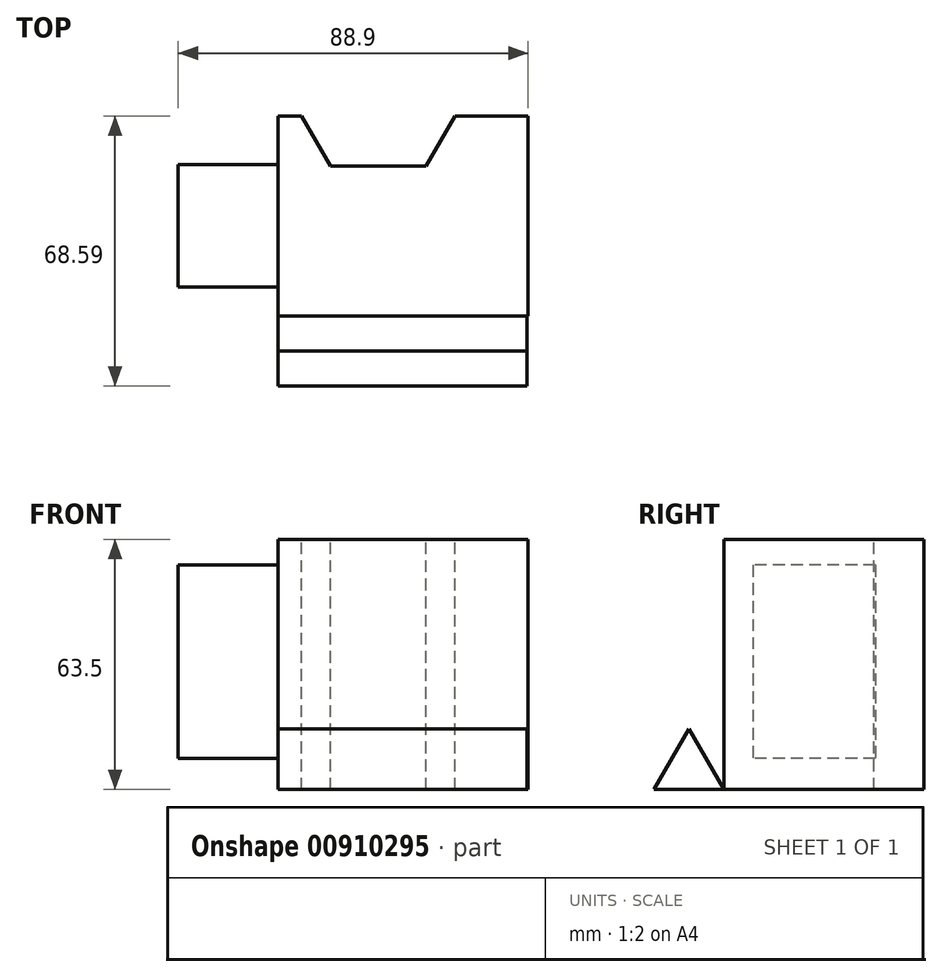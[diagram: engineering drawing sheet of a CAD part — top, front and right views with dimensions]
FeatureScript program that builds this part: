
annotation { "Feature Type Name" : "Feature", "Feature Type Description" : "" }
export const myFeature = defineFeature(function(context is Context, id is Id, definition is map)
    precondition{}
    {
        {
            var Q0;
            Q0=qCreatedBy(makeId("Front.planeOp"),FACE);
            var sketch = newSketch(context, id + "F0", { "sketchPlane" : qUnion([Q0])});
            skLineSegment(sketch, "E0.bottom", {"start": v(-31.75, 31.75) * mm, "end": v(31.75, 31.75) * mm});
            skLineSegment(sketch, "E0.top", {"start": v(-31.75, -31.75) * mm, "end": v(31.75, -31.75) * mm});
            skLineSegment(sketch, "E0.left", {"start": v(-31.75, 31.75) * mm, "end": v(-31.75, -31.75) * mm});
            skLineSegment(sketch, "E0.right", {"start": v(31.75, 31.75) * mm, "end": v(31.75, -31.75) * mm});
            skPoint(sketch, "E0.middle", {"position": v(0, 0) * mm});
            skSolve(sketch);
        }
        {
            var Q0;
            Q0=makeQuery(id+"F0.imprint","IMPRINT",FACE,{"disambiguationData":[TD([[makeQuery(id+"F0.imprint","IMPRINT",EDGE,{"derivedFrom":sQuery(id+"F0.wireOp",EDGE,"E0.bottom")}),-1.0]])]});
            extrude(context, id + "F1", {"entities" : qUnion([Q0]), "depth" : 50.8 * mm, "offsetDistance" : 25.4 * mm});
        }
        {
            var Q0;
            Q0=makeQuery(id+"F1.opExtrude","SWEPT_FACE",FACE,{"disambiguationData":[OSD([sQuery(id+"F0.wireOp",EDGE,"E0.bottom")])]});
            var sketch = newSketch(context, id + "F2", { "sketchPlane" : qUnion([Q0])});
            skLineSegment(sketch, "E1", {"start": v(-25.83, 0) * mm, "end": v(-18.5, -12.7) * mm});
            skLineSegment(sketch, "E2", {"start": v(-18.5, -12.7) * mm, "end": v(5.8, -12.7) * mm});
            skLineSegment(sketch, "E3", {"start": v(5.8, -12.7) * mm, "end": v(13.13, 0) * mm});
            skLineSegment(sketch, "E4", {"start": v(13.13, 0) * mm, "end": v(-25.83, 0) * mm});
            skLineSegment(sketch, "E5", {"start": v(-6.35, -12.7) * mm, "end": v(-6.35, 0) * mm, "construction": true});
            skSolve(sketch);
        }
        {
            var Q0;
            Q0=makeQuery(id+"F2.imprint","IMPRINT",FACE,{"disambiguationData":[TD([[makeQuery(id+"F2.imprint","IMPRINT",EDGE,{"derivedFrom":sQuery(id+"F2.wireOp",EDGE,"E1")}),1.0]])]});
            extrude(context, id + "F3", {"entities" : qUnion([Q0]), "operationType" : NewBodyOperationType.REMOVE, "oppositeDirection" : true, "depth" : 82.04 * mm, "offsetDistance" : 25.4 * mm});
        }
        {
            var Q0;
            Q0=makeQuery(id+"F1.opExtrude","SWEPT_FACE",FACE,{"disambiguationData":[OSD([sQuery(id+"F0.wireOp",EDGE,"E0.left")])]});
            var sketch = newSketch(context, id + "F4", { "sketchPlane" : qUnion([Q0])});
            skSolve(sketch);
        }
        {
            var Q0;
            {var subQ0=sQuery(id+"F0.wireOp",EDGE,"E0.left");Q0=makeQuery(id+"F4.imprint","IMPRINT",FACE,{"disambiguationData":[TD([[makeQuery(id+"F4.imprint","IMPRINT",EDGE,{"derivedFrom":makeQuery(id+"F1.opExtrude","CAP_EDGE",EDGE,{"disambiguationData":[OSD([subQ0])],"isStart":true})}),1.0]])]});}
            var sketch = newSketch(context, id + "F5", { "sketchPlane" : qUnion([Q0])});
            skLineSegment(sketch, "E6", {"start": v(50.8, -31.75) * mm, "end": v(59.7, -16.34) * mm});
            skLineSegment(sketch, "E7", {"start": v(59.7, -16.34) * mm, "end": v(68.6, -31.75) * mm});
            skLineSegment(sketch, "E8", {"start": v(68.6, -31.75) * mm, "end": v(50.8, -31.75) * mm});
            skSolve(sketch);
        }
        {
            var Q0;
            Q0 = qSketchRegion(id + "F5", true);
            extrude(context, id + "F6", {"entities" : qUnion([Q0]), "oppositeDirection" : true, "depth" : 63.25 * mm, "offsetDistance" : 25.4 * mm});
        }
        {
            var Q0;
            {var subQ0=sQuery(id+"F0.wireOp",EDGE,"E0.left");Q0=makeQuery(id+"F4.imprint","IMPRINT",FACE,{"disambiguationData":[TD([[makeQuery(id+"F4.imprint","IMPRINT",EDGE,{"derivedFrom":makeQuery(id+"F1.opExtrude","CAP_EDGE",EDGE,{"disambiguationData":[OSD([subQ0])],"isStart":true})}),1.0]])]});}
            var sketch = newSketch(context, id + "F7", { "sketchPlane" : qUnion([Q0])});
            skLineSegment(sketch, "E9.bottom", {"start": v(12.38, 25.3) * mm, "end": v(43.44, 25.3) * mm});
            skLineSegment(sketch, "E9.top", {"start": v(12.38, -23.8) * mm, "end": v(43.44, -23.8) * mm});
            skLineSegment(sketch, "E9.left", {"start": v(12.38, 25.3) * mm, "end": v(12.38, -23.8) * mm});
            skLineSegment(sketch, "E9.right", {"start": v(43.44, 25.3) * mm, "end": v(43.44, -23.8) * mm});
            skSolve(sketch);
        }
        {
            var Q0;
            Q0 = qSketchRegion(id + "F7", true);
            extrude(context, id + "F8", {"entities" : qUnion([Q0]), "operationType" : NewBodyOperationType.ADD, "depth" : 25.4 * mm, "offsetDistance" : 25.4 * mm});
        }
    });
